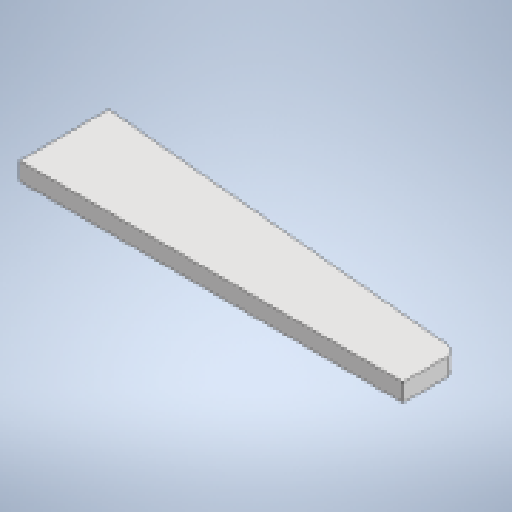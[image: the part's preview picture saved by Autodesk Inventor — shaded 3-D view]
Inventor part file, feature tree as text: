
AUTODESK INVENTOR PART (.ipt)
format: ipt  version: 2025.4 (Build 294407000, 407)  size: 162,816 bytes
history: native  units: mm
features: other x2, sheet_metal_op x1, chamfer x1, sketch x1
ambient origin geometry x8: Origin, YZ Plane, XZ Plane, XY Plane, X Axis, Y Axis, Z Axis, Center Point
bodies: Body1 (feature_tree)
feature tree (5):
  sheet_metal_op  "Face1"
  chamfer  "Corner Round1"
  sketch  "Sketch3"  dims[d11=260.0mm d12=30.0mm d13=45.0mm d14=50.0mm d15=10.0mm d16=6.0mm]
  other  "Plate1"
  other  "Definition1"
